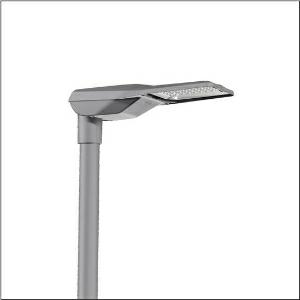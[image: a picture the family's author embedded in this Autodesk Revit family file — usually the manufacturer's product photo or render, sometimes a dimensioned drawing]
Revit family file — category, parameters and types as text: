
# Revit family: streetlight_sl_21_iq_mini___stw1_0a_5xe2e31g08hb_9864
name_source: partatom
category: Lighting Fixtures
units: mm (PartAtom-declared; Revit-internal decimal feet)

## family parameters
Cut with Voids When Loaded = No
Host = Face
Light Source = No
Part Type = Normal
Room Calculation Point = No
Round Connector Dimension = Use Diameter
Shared = No

## types (1)
- --- (1 x LED, 9450 lm, 70.9 W, 3000K)
    Apparent Load = 71 VA
    CIE Flux Codes = 38 75 98 100 100
    Color Rendering = 70
    Color Temperature = 3000K
    Default Elevation = 1800 mm
    Description = Streetlight SL 21 iQ mini, mast luminaire, primary light control with lens, of PMMA, primary optical cover: cover, of toughened safety glass, transparent, light distribution: STW1.0a, light emission: direct distribution, primary light characteristic: asymmetric, installation type: post-top, side-entry, LED, High Power LED, rated luminous flux: 9.450lm, luminous efficacy: 133lm/W, light colour: 730, colour temperature: 3000K, control gear: iQ Street-Remote, control: Street-Remote, Auto-Match, Temp-Guard, Lumen-Switch, Night-Set, Smart-Wire, Light-Fading, Desk-Remote (wireless, voltage-free reading and setting of iQ features in the workshop via application-optimized NFC function/RFID function), optimised constant luminous flux control (CLO 2.0), pre-setting: linear dimming characteristic, mains connection: 220..240V, AC, 50/60Hz, start of lifetime: 71W, end of service life: 75W, reduction: 31W, luminaire housing, of diecast aluminium, powder-coated, Siteco® metallic grey (DB 702S), corrosivity category C5 mid according to DIN EN ISO 12944, please order mast flange separately, inclination adjustable: 0°, 5°, 10°, 15°, sealing non-destructively replaceable, multi-level sealing system, length: 628mm, width: 235mm, height: 110mm, mast flange for spigot size: 42mm (side-entry): 5XC10008XM4, 60/48mm (side-entry/post-top): 5XC10108XM2, 76/60mm (side-entry/post-top): 5XC10108XM1, mounting height: 4..8m, protection rating (complete): IP66, insulation class (complete): insulation class II (safety insulation), certification: CE, ENEC, ENEC+, VDE, impact resistance: IK10, permissible operating ambient temperature for outdoor applications: -40..+50°C, standard-compliant lighting for roads and squares, packaging unit: 1 piece

Light Distribution: STW1.0a
    Height = 110 mm
    Lamp = 1 x LED
    Lamp Light Flux = 9450 lm
    Lamp Power = 70.9 W
    Lamp count = 1
    Length = 625 mm
    Luminous efficacy = 133 lm/W
    Manufacturer = Siteco
    ModVariant = No
    Model = 5XE2E31G08HB
    Number of Poles = 1
    OnlyDefault = Yes
    Power Factor = 1
    Product Name = Streetlight SL 21 iQ mini | STW1.0a
    Product group = mast luminaire | pylon top
    ProductGroupID = 6100
    Protection Class = Protection class II
    Protection Degree = IP 66
    RLX_Detail_Level = 1
    RLX_Emergency_Light_Flux = 0 lm
    RLX_Emergency_Type = 0
    RLX_Emergency_Type_DB = No
    RlxData = <blob elided: 26433 chars, md5=2dc66321>
    Socket = socket
    Standby Power = 0 W
    System Light Flux = 9450 lm
    System Power = 71 W
    Type Comments = factory setting: luminous flux: 100 % | dim-lin: 254 | 711 mA
    Type Image = l_1003519.jpg
    URL = http://relux.com
    VarID = @adj_157846
    Voltage = 0 V
    Weight = 0.00 kg
    Width = 234 mm

## geometry (parser evidence)
native form markers: Blend x4, Sweep x9
no freeform markers — native parametric forms only
